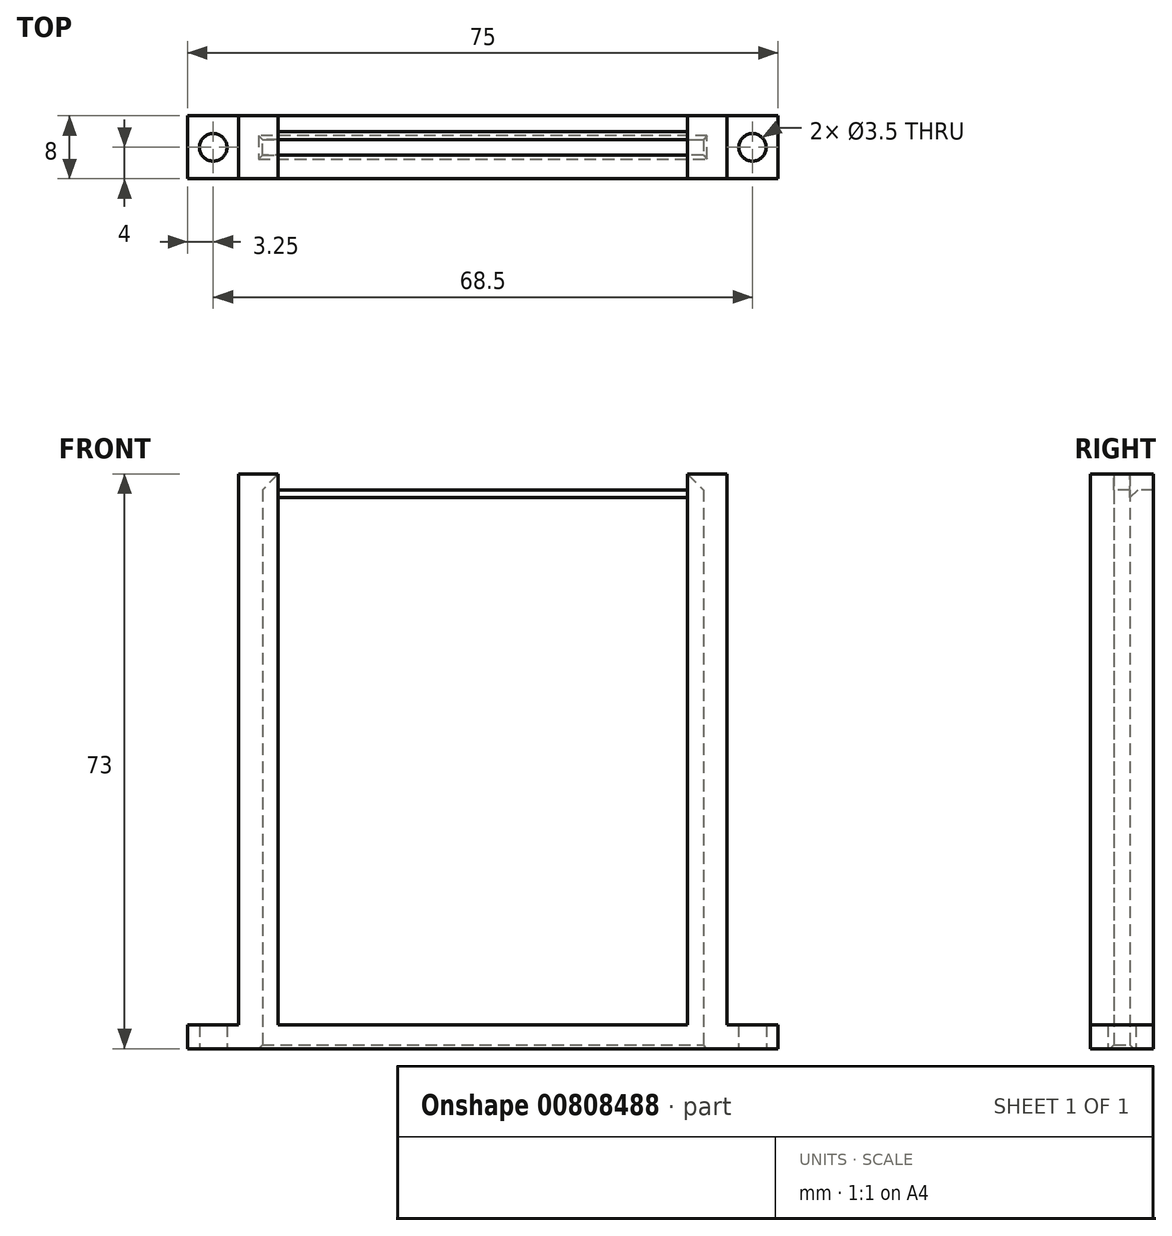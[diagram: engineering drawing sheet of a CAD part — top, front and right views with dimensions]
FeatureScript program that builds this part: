
annotation { "Feature Type Name" : "Feature", "Feature Type Description" : "" }
export const myFeature = defineFeature(function(context is Context, id is Id, definition is map)
    precondition{}
    {
        {
            var Q0;
            Q0=qCreatedBy(makeId("Top.planeOp"),FACE);
            var sketch = newSketch(context, id + "F0", { "sketchPlane" : qUnion([Q0])});
            skLineSegment(sketch, "E0.bottom", {"start": v(-37.5, 4) * mm, "end": v(37.5, 4) * mm});
            skLineSegment(sketch, "E0.top", {"start": v(-37.5, -4) * mm, "end": v(37.5, -4) * mm});
            skLineSegment(sketch, "E0.left", {"start": v(-37.5, 4) * mm, "end": v(-37.5, -4) * mm});
            skLineSegment(sketch, "E0.right", {"start": v(37.5, 4) * mm, "end": v(37.5, -4) * mm});
            skPoint(sketch, "E0.middle", {"position": v(0, 0) * mm});
            skLineSegment(sketch, "E1.bottom", {"start": v(-28, 1) * mm, "end": v(28, 1) * mm});
            skLineSegment(sketch, "E1.top", {"start": v(-28, -1) * mm, "end": v(28, -1) * mm});
            skLineSegment(sketch, "E1.left", {"start": v(-28, 1) * mm, "end": v(-28, -1) * mm});
            skLineSegment(sketch, "E1.right", {"start": v(28, 1) * mm, "end": v(28, -1) * mm});
            skCircle(sketch, "E2", {"center": v(-34.25, 0) * mm, "radius": 1.75 * mm});
            skCircle(sketch, "E3", {"center": v(34.25, 0) * mm, "radius": 1.75 * mm});
            skSolve(sketch);
        }
        {
            var Q0;
            Q0 = qSketchRegion(id + "F0", true);
            extrude(context, id + "F1", {"entities" : qUnion([Q0]), "depth" : 3 * mm, "offsetDistance" : 25 * mm});
        }
        {
            var Q0;
            Q0=makeQuery(id+"F1.opExtrude","CAP_FACE",FACE,{"disambiguationData":[OSD([sQuery(id+"F0.wireOp",EDGE,"E0.bottom"),sQuery(id+"F0.wireOp",EDGE,"E0.top"),sQuery(id+"F0.wireOp",EDGE,"E0.left"),sQuery(id+"F0.wireOp",EDGE,"E0.right"),sQuery(id+"F0.wireOp",EDGE,"E1.bottom"),sQuery(id+"F0.wireOp",EDGE,"E1.top"),sQuery(id+"F0.wireOp",EDGE,"E1.left"),sQuery(id+"F0.wireOp",EDGE,"E1.right"),sQuery(id+"F0.wireOp",EDGE,"E2"),sQuery(id+"F0.wireOp",EDGE,"E3")])],"isStart":false});
            var sketch = newSketch(context, id + "F2", { "sketchPlane" : qUnion([Q0])});
            skLineSegment(sketch, "E4.0", {"start": v(-31, -4) * mm, "end": v(31, -4) * mm});
            skLineSegment(sketch, "E4.1", {"start": v(-31, 4) * mm, "end": v(-31, -4) * mm});
            skLineSegment(sketch, "E4.2", {"start": v(-31, 4) * mm, "end": v(31, 4) * mm});
            skLineSegment(sketch, "E4.3", {"start": v(31, 4) * mm, "end": v(31, -4) * mm});
            skLineSegment(sketch, "E5.bottom", {"start": v(-26, -1) * mm, "end": v(26, -1) * mm});
            skLineSegment(sketch, "E5.top", {"start": v(-26, -4) * mm, "end": v(26, -4) * mm});
            skLineSegment(sketch, "E5.left", {"start": v(-26, -1) * mm, "end": v(-26, -4) * mm});
            skLineSegment(sketch, "E5.right", {"start": v(26, -1) * mm, "end": v(26, -4) * mm});
            skSolve(sketch);
        }
        {
            var Q0;
            {var subQ3=sQuery(id+"F2.wireOp",EDGE,"E4.1");Q0=makeQuery(id+"F2.imprint","IMPRINT",FACE,{"disambiguationData":[TD([[makeQuery(id+"F2.imprint","IMPRINT",EDGE,{"derivedFrom":subQ3}),1.0]])]});}
            extrude(context, id + "F3", {"entities" : qUnion([Q0]), "operationType" : NewBodyOperationType.ADD, "depth" : 68 * mm, "offsetDistance" : 25 * mm});
        }
        {
            var Q0;
            Q0=makeQuery(id+"F3.opExtrude","CAP_FACE",FACE,{"disambiguationData":[OSD([sQuery(id+"F0.wireOp",EDGE,"E1.bottom"),sQuery(id+"F0.wireOp",EDGE,"E1.top"),sQuery(id+"F0.wireOp",EDGE,"E1.left"),sQuery(id+"F0.wireOp",EDGE,"E1.right"),sQuery(id+"F2.wireOp",EDGE,"E4.0"),sQuery(id+"F2.wireOp",EDGE,"E4.1"),sQuery(id+"F2.wireOp",EDGE,"E4.2"),sQuery(id+"F2.wireOp",EDGE,"E4.3"),sQuery(id+"F2.wireOp",EDGE,"E5.left"),sQuery(id+"F2.wireOp",EDGE,"E5.right")])],"isStart":false});
            var sketch = newSketch(context, id + "F4", { "sketchPlane" : qUnion([Q0])});
            skLineSegment(sketch, "E6.bottom", {"start": v(-31, 4) * mm, "end": v(-26, 4) * mm});
            skLineSegment(sketch, "E6.top", {"start": v(-31, -4) * mm, "end": v(-26, -4) * mm});
            skLineSegment(sketch, "E6.left", {"start": v(-31, 4) * mm, "end": v(-31, -4) * mm});
            skLineSegment(sketch, "E6.right", {"start": v(-26, 4) * mm, "end": v(-26, -4) * mm});
            skLineSegment(sketch, "E7.bottom", {"start": v(31, 4) * mm, "end": v(26, 4) * mm});
            skLineSegment(sketch, "E7.top", {"start": v(31, -4) * mm, "end": v(26, -4) * mm});
            skLineSegment(sketch, "E7.left", {"start": v(31, 4) * mm, "end": v(31, -4) * mm});
            skLineSegment(sketch, "E7.right", {"start": v(26, 4) * mm, "end": v(26, -4) * mm});
            skSolve(sketch);
        }
        {
            var Q0;
            Q0 = qSketchRegion(id + "F4", true);
            extrude(context, id + "F5", {"entities" : qUnion([Q0]), "operationType" : NewBodyOperationType.ADD, "depth" : 2 * mm, "offsetDistance" : 25 * mm});
        }
        {
            var Q0;
            {var subQ0=sQuery(id+"F2.wireOp",EDGE,"E5.left");var subQ1=sQuery(id+"F4.wireOp",EDGE,"E6.right");Q0=makeQuery(id+"F5.boolean.opBoolean","SPLIT",EDGE,{"disambiguationData":[topologyDisambiguationEdgeConnected([makeQuery(id+"F3.opExtrude","CAP_FACE",FACE,{"disambiguationData":[OSD([sQuery(id+"F0.wireOp",EDGE,"E1.bottom"),sQuery(id+"F0.wireOp",EDGE,"E1.top"),sQuery(id+"F0.wireOp",EDGE,"E1.left"),sQuery(id+"F0.wireOp",EDGE,"E1.right"),sQuery(id+"F2.wireOp",EDGE,"E4.0"),sQuery(id+"F2.wireOp",EDGE,"E4.1"),sQuery(id+"F2.wireOp",EDGE,"E4.2"),sQuery(id+"F2.wireOp",EDGE,"E4.3"),subQ0,sQuery(id+"F2.wireOp",EDGE,"E5.right")])],"isStart":false})])],"derivedFrom":makeQuery(id+"F5.opExtrude","CAP_EDGE",EDGE,{"disambiguationData":[OSD([subQ1])],"isStart":true})});}
            var Q1;
            {var subQ0=sQuery(id+"F2.wireOp",EDGE,"E5.right");var subQ1=sQuery(id+"F4.wireOp",EDGE,"E7.right");Q1=makeQuery(id+"F5.boolean.opBoolean","SPLIT",EDGE,{"disambiguationData":[topologyDisambiguationEdgeConnected([makeQuery(id+"F3.opExtrude","CAP_FACE",FACE,{"disambiguationData":[OSD([sQuery(id+"F0.wireOp",EDGE,"E1.bottom"),sQuery(id+"F0.wireOp",EDGE,"E1.top"),sQuery(id+"F0.wireOp",EDGE,"E1.left"),sQuery(id+"F0.wireOp",EDGE,"E1.right"),sQuery(id+"F2.wireOp",EDGE,"E4.0"),sQuery(id+"F2.wireOp",EDGE,"E4.1"),sQuery(id+"F2.wireOp",EDGE,"E4.2"),sQuery(id+"F2.wireOp",EDGE,"E4.3"),sQuery(id+"F2.wireOp",EDGE,"E5.left"),subQ0])],"isStart":false})])],"derivedFrom":makeQuery(id+"F5.opExtrude","CAP_EDGE",EDGE,{"disambiguationData":[OSD([subQ1])],"isStart":true})});}
            chamfer(context, id + "F6", {"entities" : qUnion([Q0, Q1]), "width" : 2 * mm, "tangentPropagation" : true});
        }
        {
            var Q0;
            {var subQ0=sQuery(id+"F0.wireOp",EDGE,"E1.bottom");Q0=makeQuery(id+"F5.boolean.opBoolean","SPLIT",EDGE,{"disambiguationData":[topologyDisambiguationEdgeConnected([makeQuery(id+"F5.opExtrude","CAP_FACE",FACE,{"disambiguationData":[OSD([sQuery(id+"F4.wireOp",EDGE,"E6.bottom"),sQuery(id+"F4.wireOp",EDGE,"E6.top"),sQuery(id+"F4.wireOp",EDGE,"E6.left"),sQuery(id+"F4.wireOp",EDGE,"E6.right")])],"isStart":true})])],"derivedFrom":makeQuery(id+"F3.opExtrude","CAP_EDGE",EDGE,{"disambiguationData":[OSD([subQ0])],"isStart":false})});}
            var Q1;
            {var subQ0=sQuery(id+"F0.wireOp",EDGE,"E1.bottom");Q1=makeQuery(id+"F5.boolean.opBoolean","SPLIT",EDGE,{"disambiguationData":[topologyDisambiguationEdgeConnected([makeQuery(id+"F5.opExtrude","CAP_FACE",FACE,{"disambiguationData":[OSD([sQuery(id+"F4.wireOp",EDGE,"E7.bottom"),sQuery(id+"F4.wireOp",EDGE,"E7.top"),sQuery(id+"F4.wireOp",EDGE,"E7.left"),sQuery(id+"F4.wireOp",EDGE,"E7.right")])],"isStart":true})])],"derivedFrom":makeQuery(id+"F3.opExtrude","CAP_EDGE",EDGE,{"disambiguationData":[OSD([subQ0])],"isStart":false})});}
            var Q2;
            {var subQ0=sQuery(id+"F0.wireOp",EDGE,"E1.top");var subQ1=makeQuery(id+"F1.opExtrude","CAP_EDGE",EDGE,{"disambiguationData":[OSD([subQ0])],"isStart":false});Q2=makeQuery(id+"F3.opExtrude","CAP_EDGE",EDGE,{"disambiguationData":[OSD([subQ0]),TDD([makeQuery(id+"F2.imprint","IMPRINT",EDGE,{"disambiguationData":[TD([[makeQuery(id+"F2.imprint","INTERSECT",VERTEX,{"derivedFrom":[subQ1,makeQuery(id+"F1.opExtrude","CAP_EDGE",EDGE,{"disambiguationData":[OSD([sQuery(id+"F0.wireOp",EDGE,"E1.right")])],"isStart":false})]}),1.0]])],"derivedFrom":subQ1})])],"isStart":false});}
            var Q3;
            {var subQ0=sQuery(id+"F0.wireOp",EDGE,"E1.top");var subQ1=makeQuery(id+"F1.opExtrude","CAP_EDGE",EDGE,{"disambiguationData":[OSD([subQ0])],"isStart":false});Q3=makeQuery(id+"F3.opExtrude","CAP_EDGE",EDGE,{"disambiguationData":[OSD([subQ0]),TDD([makeQuery(id+"F2.imprint","IMPRINT",EDGE,{"disambiguationData":[TD([[makeQuery(id+"F2.imprint","INTERSECT",VERTEX,{"derivedFrom":[subQ1,makeQuery(id+"F1.opExtrude","CAP_EDGE",EDGE,{"disambiguationData":[OSD([sQuery(id+"F0.wireOp",EDGE,"E1.left")])],"isStart":false})]}),-1.0]])],"derivedFrom":subQ1})])],"isStart":false});}
            chamfer(context, id + "F7", {"entities" : qUnion([Q0, Q1, Q2, Q3]), "width" : 1 * mm, "tangentPropagation" : true});
        }
        {
            var Q0;
            Q0=makeQuery(id+"F1.opExtrude","CAP_EDGE",EDGE,{"disambiguationData":[OSD([sQuery(id+"F0.wireOp",EDGE,"E1.top")])],"isStart":true});
            var Q1;
            Q1=makeQuery(id+"F1.opExtrude","CAP_EDGE",EDGE,{"disambiguationData":[OSD([sQuery(id+"F0.wireOp",EDGE,"E1.bottom")])],"isStart":true});
            var Q2;
            Q2=makeQuery(id+"F1.opExtrude","CAP_EDGE",EDGE,{"disambiguationData":[OSD([sQuery(id+"F0.wireOp",EDGE,"E1.left")])],"isStart":true});
            var Q3;
            Q3=makeQuery(id+"F1.opExtrude","CAP_EDGE",EDGE,{"disambiguationData":[OSD([sQuery(id+"F0.wireOp",EDGE,"E1.right")])],"isStart":true});
            chamfer(context, id + "F8", {"entities" : qUnion([Q0, Q1, Q2, Q3]), "width" : 0.5 * mm, "tangentPropagation" : true});
        }
    });
